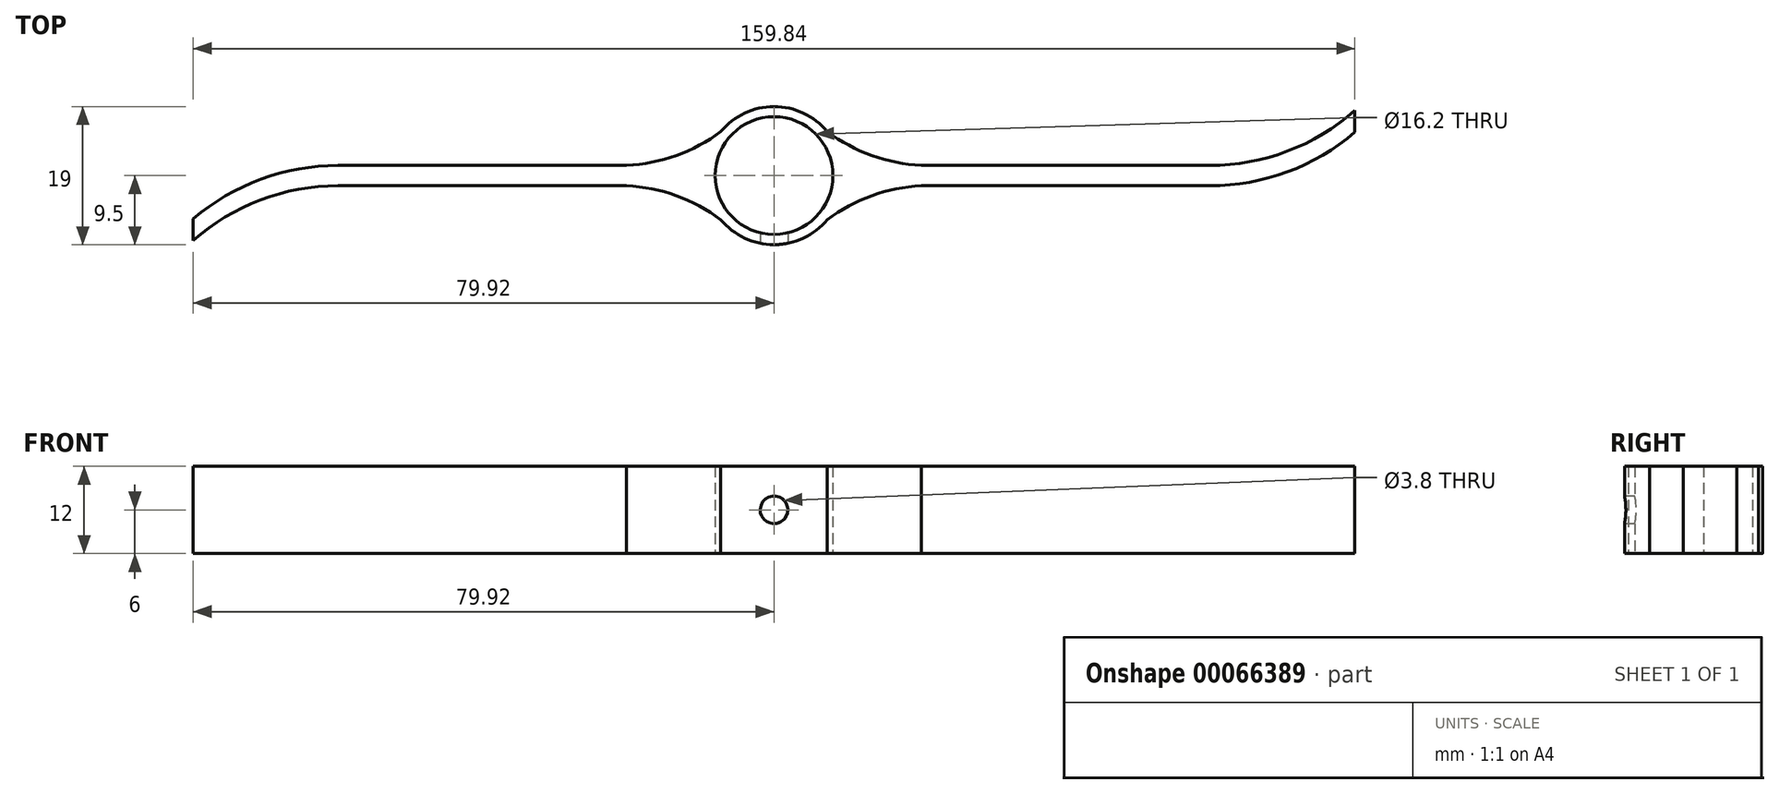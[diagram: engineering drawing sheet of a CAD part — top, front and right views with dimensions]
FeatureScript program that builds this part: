
annotation { "Feature Type Name" : "Feature", "Feature Type Description" : "" }
export const myFeature = defineFeature(function(context is Context, id is Id, definition is map)
    precondition{}
    {
        {
            var Q0;
            Q0=qCreatedBy(makeId("Top.planeOp"),FACE);
            var sketch = newSketch(context, id + "F0", { "sketchPlane" : qUnion([Q0])});
            skCircle(sketch, "E0", {"center": v(0, 0) * mm, "radius": 8.1 * mm});
            skArc(sketch, "E1", {"start": v(7.32, 6.05) * mm, "mid": v(0, 9.5) * mm, "end": v(-7.32, 6.05) * mm});
            skLineSegment(sketch, "E2", {"start": v(0, 0) * mm, "end": v(80, 0) * mm, "construction": true});
            skLineSegment(sketch, "E3", {"start": v(0, 0) * mm, "end": v(0, 1.4) * mm, "construction": true});
            skLineSegment(sketch, "E4", {"start": v(20.27, 1.4) * mm, "end": v(60, 1.4) * mm});
            skArc(sketch, "E5", {"start": v(60, 1.4) * mm, "mid": v(70.65, 3.35) * mm, "end": v(79.92, 8.96) * mm});
            skLineSegment(sketch, "E6.MirrorCS", {"start": v(20.27, -1.4) * mm, "end": v(60, -1.4) * mm});
            skLineSegment(sketch, "E7", {"start": v(79.92, 8.96) * mm, "end": v(79.92, 5.96) * mm});
            skArc(sketch, "E8", {"start": v(60, -1.4) * mm, "mid": v(70.62, 0.5) * mm, "end": v(79.92, 5.96) * mm});
            skPoint(sketch, "E9.orphan", {"position": v(0, -1.4) * mm});
            skArc(sketch, "E10", {"start": v(7.32, 6.05) * mm, "mid": v(13.45, 2.76) * mm, "end": v(20.27, 1.4) * mm});
            skArc(sketch, "E11.MirrorCS", {"start": v(7.32, -6.05) * mm, "mid": v(13.45, -2.76) * mm, "end": v(20.27, -1.4) * mm});
            skArc(sketch, "E12.1.0", {"start": v(-7.32, -6.05) * mm, "mid": v(-13.45, -2.76) * mm, "end": v(-20.27, -1.4) * mm});
            skArc(sketch, "E12.1.1", {"start": v(-60, 1.4) * mm, "mid": v(-70.62, -0.5) * mm, "end": v(-79.92, -5.96) * mm});
            skArc(sketch, "E12.1.2", {"start": v(-7.32, 6.05) * mm, "mid": v(-13.45, 2.76) * mm, "end": v(-20.27, 1.4) * mm});
            skArc(sketch, "E12.1.3", {"start": v(-60, -1.4) * mm, "mid": v(-70.65, -3.35) * mm, "end": v(-79.92, -8.96) * mm});
            skLineSegment(sketch, "E12.1.4", {"start": v(-20.27, 1.4) * mm, "end": v(-60, 1.4) * mm});
            skLineSegment(sketch, "E12.1.5", {"start": v(-20.27, -1.4) * mm, "end": v(-60, -1.4) * mm});
            skLineSegment(sketch, "E12.1.6", {"start": v(0, 0) * mm, "end": v(-80, 0) * mm, "construction": true});
            skLineSegment(sketch, "E12.1.7", {"start": v(-79.92, -8.96) * mm, "end": v(-79.92, -5.96) * mm});
            skArc(sketch, "E12.1.8", {"start": v(-7.32, -6.05) * mm, "mid": v(0, -9.5) * mm, "end": v(7.32, -6.05) * mm});
            skSolve(sketch);
        }
        {
            var Q0;
            Q0=makeQuery(id+"F0.imprint","IMPRINT",FACE,{"disambiguationData":[TD([[makeQuery(id+"F0.imprint","IMPRINT",EDGE,{"derivedFrom":sQuery(id+"F0.wireOp",EDGE,"E0")}),-1.0]])]});
            extrude(context, id + "F1", {"entities" : qUnion([Q0]), "depth" : 12 * mm});
        }
        {
            var Q0;
            Q0=qCreatedBy(makeId("Front.planeOp"),FACE);
            cPlane(context, id + "F2", {"entities" : qUnion([Q0]), "cplaneType" : CPlaneType.OFFSET, "offset" : 9.5 * mm, "width" : 150 * mm, "height" : 150 * mm});
        }
        {
            var Q0;
            Q0=qCreatedBy(id+"F2.planeOp",FACE);
            var sketch = newSketch(context, id + "F3", { "sketchPlane" : qUnion([Q0])});
            skLineSegment(sketch, "E13", {"start": v(0, 0) * mm, "end": v(0, 6) * mm, "construction": true});
            skCircle(sketch, "E14", {"center": v(0, 6) * mm, "radius": 1.9 * mm});
            skSolve(sketch);
        }
        {
            var Q0;
            Q0=makeQuery(id+"F3.imprint","IMPRINT",FACE,{"disambiguationData":[TD([[makeQuery(id+"F3.imprint","IMPRINT",EDGE,{"derivedFrom":sQuery(id+"F3.wireOp",EDGE,"E14")}),1.0]])]});
            extrude(context, id + "F4", {"entities" : qUnion([Q0]), "operationType" : NewBodyOperationType.REMOVE, "oppositeDirection" : true, "depth" : 8 * mm});
        }
    });
